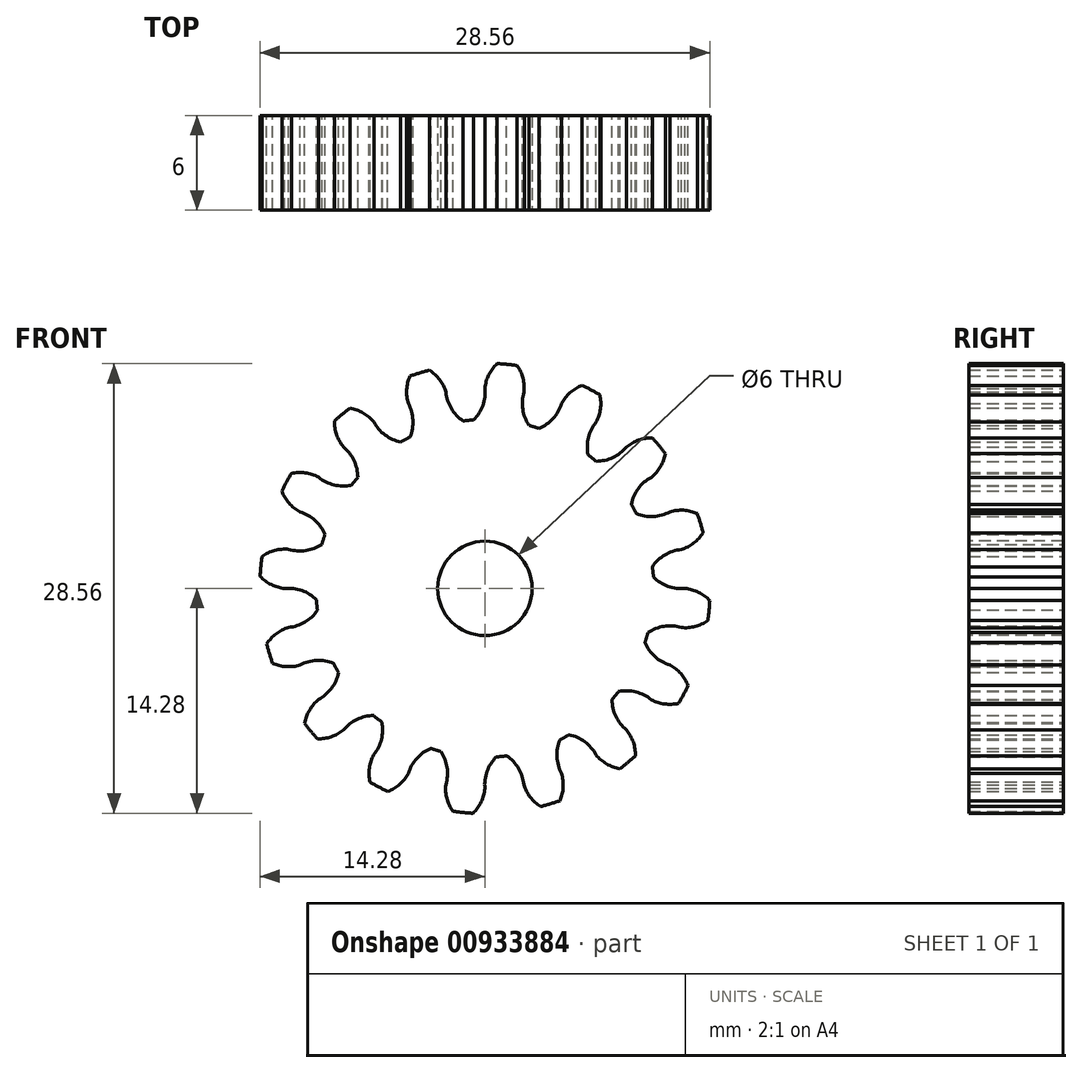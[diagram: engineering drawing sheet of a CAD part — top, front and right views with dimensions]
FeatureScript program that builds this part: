
annotation { "Feature Type Name" : "Feature", "Feature Type Description" : "" }
export const myFeature = defineFeature(function(context is Context, id is Id, definition is map)
    precondition{}
    {
        {
            var Q0;
            Q0=qCreatedBy(makeId("Front.planeOp"),FACE);
            var sketch = newSketch(context, id + "F0", { "sketchPlane" : qUnion([Q0])});
            skArc(sketch, "E0", {"start": v(2.04, 14.15) * mm, "mid": v(1.4, 14.23) * mm, "end": v(0.77, 14.28) * mm});
            skCircle(sketch, "E1", {"center": v(0, 0) * mm, "radius": 10.73 * mm});
            skArc(sketch, "E2", {"start": v(2.49, 12.47) * mm, "mid": v(2.41, 13.35) * mm, "end": v(2.04, 14.15) * mm});
            skArc(sketch, "E3", {"start": v(2.49, 12.47) * mm, "mid": v(2.4, 11.38) * mm, "end": v(2.8, 10.35) * mm});
            skArc(sketch, "E4", {"start": v(-0.72, 10.7) * mm, "mid": v(-0.13, 11.63) * mm, "end": v(0, 12.71) * mm});
            skArc(sketch, "E5.trimOffspring", {"start": v(0.77, 14.28) * mm, "mid": v(0.24, 13.57) * mm, "end": v(0, 12.71) * mm});
            skArc(sketch, "E6.1.0", {"start": v(-3.53, 13.86) * mm, "mid": v(-4.15, 13.69) * mm, "end": v(-4.75, 13.49) * mm});
            skArc(sketch, "E6.1.1", {"start": v(-4.75, 13.49) * mm, "mid": v(-4.97, 12.63) * mm, "end": v(-4.86, 11.74) * mm});
            skArc(sketch, "E6.1.2", {"start": v(-4.76, 9.61) * mm, "mid": v(-4.57, 10.7) * mm, "end": v(-4.86, 11.74) * mm});
            skArc(sketch, "E6.1.3", {"start": v(-2.47, 12.47) * mm, "mid": v(-2.88, 13.26) * mm, "end": v(-3.53, 13.86) * mm});
            skArc(sketch, "E6.1.4", {"start": v(-2.47, 12.47) * mm, "mid": v(-2.13, 11.43) * mm, "end": v(-1.38, 10.64) * mm});
            skArc(sketch, "E6.2.0", {"start": v(-8.57, 11.45) * mm, "mid": v(-9.07, 11.06) * mm, "end": v(-9.55, 10.64) * mm});
            skArc(sketch, "E6.2.1", {"start": v(-9.55, 10.64) * mm, "mid": v(-9.42, 9.76) * mm, "end": v(-8.99, 8.99) * mm});
            skArc(sketch, "E6.2.2", {"start": v(-8.08, 7.06) * mm, "mid": v(-8.32, 8.13) * mm, "end": v(-8.99, 8.99) * mm});
            skArc(sketch, "E6.2.3", {"start": v(-7.06, 10.57) * mm, "mid": v(-7.73, 11.15) * mm, "end": v(-8.57, 11.45) * mm});
            skArc(sketch, "E6.2.4", {"start": v(-7.06, 10.57) * mm, "mid": v(-6.34, 9.74) * mm, "end": v(-5.34, 9.3) * mm});
            skArc(sketch, "E6.3.0", {"start": v(-12.3, 7.3) * mm, "mid": v(-12.61, 6.74) * mm, "end": v(-12.9, 6.17) * mm});
            skArc(sketch, "E6.3.1", {"start": v(-12.9, 6.17) * mm, "mid": v(-12.44, 5.42) * mm, "end": v(-11.74, 4.86) * mm});
            skArc(sketch, "E6.3.2", {"start": v(-10.16, 3.43) * mm, "mid": v(-10.8, 4.33) * mm, "end": v(-11.74, 4.86) * mm});
            skArc(sketch, "E6.3.3", {"start": v(-10.57, 7.07) * mm, "mid": v(-11.41, 7.34) * mm, "end": v(-12.3, 7.3) * mm});
            skArc(sketch, "E6.3.4", {"start": v(-10.57, 7.07) * mm, "mid": v(-9.59, 6.57) * mm, "end": v(-8.5, 6.55) * mm});
            skArc(sketch, "E6.4.0", {"start": v(-14.15, 2.04) * mm, "mid": v(-14.23, 1.4) * mm, "end": v(-14.28, 0.77) * mm});
            skArc(sketch, "E6.4.1", {"start": v(-14.28, 0.77) * mm, "mid": v(-13.57, 0.24) * mm, "end": v(-12.71, 0) * mm});
            skArc(sketch, "E6.4.2", {"start": v(-10.7, -0.72) * mm, "mid": v(-11.63, -0.13) * mm, "end": v(-12.71, 0) * mm});
            skArc(sketch, "E6.4.3", {"start": v(-12.47, 2.49) * mm, "mid": v(-13.35, 2.41) * mm, "end": v(-14.15, 2.04) * mm});
            skArc(sketch, "E6.4.4", {"start": v(-12.47, 2.49) * mm, "mid": v(-11.38, 2.4) * mm, "end": v(-10.35, 2.8) * mm});
            skArc(sketch, "E6.5.0", {"start": v(-13.86, -3.53) * mm, "mid": v(-13.69, -4.15) * mm, "end": v(-13.49, -4.75) * mm});
            skArc(sketch, "E6.5.1", {"start": v(-13.49, -4.75) * mm, "mid": v(-12.63, -4.97) * mm, "end": v(-11.74, -4.86) * mm});
            skArc(sketch, "E6.5.2", {"start": v(-9.61, -4.76) * mm, "mid": v(-10.7, -4.57) * mm, "end": v(-11.74, -4.86) * mm});
            skArc(sketch, "E6.5.3", {"start": v(-12.47, -2.47) * mm, "mid": v(-13.26, -2.88) * mm, "end": v(-13.86, -3.53) * mm});
            skArc(sketch, "E6.5.4", {"start": v(-12.47, -2.47) * mm, "mid": v(-11.43, -2.13) * mm, "end": v(-10.64, -1.38) * mm});
            skArc(sketch, "E6.6.0", {"start": v(-11.45, -8.57) * mm, "mid": v(-11.06, -9.07) * mm, "end": v(-10.64, -9.55) * mm});
            skArc(sketch, "E6.6.1", {"start": v(-10.64, -9.55) * mm, "mid": v(-9.76, -9.42) * mm, "end": v(-8.99, -8.99) * mm});
            skArc(sketch, "E6.6.2", {"start": v(-7.06, -8.08) * mm, "mid": v(-8.13, -8.32) * mm, "end": v(-8.99, -8.99) * mm});
            skArc(sketch, "E6.6.3", {"start": v(-10.57, -7.06) * mm, "mid": v(-11.15, -7.73) * mm, "end": v(-11.45, -8.57) * mm});
            skArc(sketch, "E6.6.4", {"start": v(-10.57, -7.06) * mm, "mid": v(-9.74, -6.34) * mm, "end": v(-9.3, -5.34) * mm});
            skArc(sketch, "E6.7.0", {"start": v(-7.3, -12.3) * mm, "mid": v(-6.74, -12.61) * mm, "end": v(-6.17, -12.9) * mm});
            skArc(sketch, "E6.7.1", {"start": v(-6.17, -12.9) * mm, "mid": v(-5.42, -12.44) * mm, "end": v(-4.86, -11.74) * mm});
            skArc(sketch, "E6.7.2", {"start": v(-3.43, -10.16) * mm, "mid": v(-4.33, -10.8) * mm, "end": v(-4.86, -11.74) * mm});
            skArc(sketch, "E6.7.3", {"start": v(-7.07, -10.57) * mm, "mid": v(-7.34, -11.41) * mm, "end": v(-7.3, -12.3) * mm});
            skArc(sketch, "E6.7.4", {"start": v(-7.07, -10.57) * mm, "mid": v(-6.57, -9.59) * mm, "end": v(-6.55, -8.5) * mm});
            skArc(sketch, "E6.8.0", {"start": v(-2.04, -14.15) * mm, "mid": v(-1.4, -14.23) * mm, "end": v(-0.77, -14.28) * mm});
            skArc(sketch, "E6.8.1", {"start": v(-0.77, -14.28) * mm, "mid": v(-0.24, -13.57) * mm, "end": v(0, -12.71) * mm});
            skArc(sketch, "E6.8.2", {"start": v(0.72, -10.7) * mm, "mid": v(0.13, -11.63) * mm, "end": v(0, -12.71) * mm});
            skArc(sketch, "E6.8.3", {"start": v(-2.49, -12.47) * mm, "mid": v(-2.41, -13.35) * mm, "end": v(-2.04, -14.15) * mm});
            skArc(sketch, "E6.8.4", {"start": v(-2.49, -12.47) * mm, "mid": v(-2.4, -11.38) * mm, "end": v(-2.8, -10.35) * mm});
            skArc(sketch, "E6.9.0", {"start": v(3.53, -13.86) * mm, "mid": v(4.15, -13.69) * mm, "end": v(4.75, -13.49) * mm});
            skArc(sketch, "E6.9.1", {"start": v(4.75, -13.49) * mm, "mid": v(4.97, -12.63) * mm, "end": v(4.86, -11.74) * mm});
            skArc(sketch, "E6.9.2", {"start": v(4.76, -9.61) * mm, "mid": v(4.57, -10.7) * mm, "end": v(4.86, -11.74) * mm});
            skArc(sketch, "E6.9.3", {"start": v(2.47, -12.47) * mm, "mid": v(2.88, -13.26) * mm, "end": v(3.53, -13.86) * mm});
            skArc(sketch, "E6.9.4", {"start": v(2.47, -12.47) * mm, "mid": v(2.13, -11.43) * mm, "end": v(1.38, -10.64) * mm});
            skArc(sketch, "E6.10.0", {"start": v(8.57, -11.45) * mm, "mid": v(9.07, -11.06) * mm, "end": v(9.55, -10.64) * mm});
            skArc(sketch, "E6.10.1", {"start": v(9.55, -10.64) * mm, "mid": v(9.42, -9.76) * mm, "end": v(8.99, -8.99) * mm});
            skArc(sketch, "E6.10.2", {"start": v(8.08, -7.06) * mm, "mid": v(8.32, -8.13) * mm, "end": v(8.99, -8.99) * mm});
            skArc(sketch, "E6.10.3", {"start": v(7.06, -10.57) * mm, "mid": v(7.73, -11.15) * mm, "end": v(8.57, -11.45) * mm});
            skArc(sketch, "E6.10.4", {"start": v(7.06, -10.57) * mm, "mid": v(6.34, -9.74) * mm, "end": v(5.34, -9.3) * mm});
            skArc(sketch, "E6.11.0", {"start": v(12.3, -7.3) * mm, "mid": v(12.61, -6.74) * mm, "end": v(12.9, -6.17) * mm});
            skArc(sketch, "E6.11.1", {"start": v(12.9, -6.17) * mm, "mid": v(12.44, -5.42) * mm, "end": v(11.74, -4.86) * mm});
            skArc(sketch, "E6.11.2", {"start": v(10.16, -3.43) * mm, "mid": v(10.8, -4.33) * mm, "end": v(11.74, -4.86) * mm});
            skArc(sketch, "E6.11.3", {"start": v(10.57, -7.07) * mm, "mid": v(11.41, -7.34) * mm, "end": v(12.3, -7.3) * mm});
            skArc(sketch, "E6.11.4", {"start": v(10.57, -7.07) * mm, "mid": v(9.59, -6.57) * mm, "end": v(8.5, -6.55) * mm});
            skArc(sketch, "E6.12.0", {"start": v(14.15, -2.04) * mm, "mid": v(14.23, -1.4) * mm, "end": v(14.28, -0.77) * mm});
            skArc(sketch, "E6.12.1", {"start": v(14.28, -0.77) * mm, "mid": v(13.57, -0.24) * mm, "end": v(12.71, 0) * mm});
            skArc(sketch, "E6.12.2", {"start": v(10.7, 0.72) * mm, "mid": v(11.63, 0.13) * mm, "end": v(12.71, 0) * mm});
            skArc(sketch, "E6.12.3", {"start": v(12.47, -2.49) * mm, "mid": v(13.35, -2.41) * mm, "end": v(14.15, -2.04) * mm});
            skArc(sketch, "E6.12.4", {"start": v(12.47, -2.49) * mm, "mid": v(11.38, -2.4) * mm, "end": v(10.35, -2.8) * mm});
            skArc(sketch, "E6.13.0", {"start": v(13.86, 3.53) * mm, "mid": v(13.69, 4.15) * mm, "end": v(13.49, 4.75) * mm});
            skArc(sketch, "E6.13.1", {"start": v(13.49, 4.75) * mm, "mid": v(12.63, 4.97) * mm, "end": v(11.74, 4.86) * mm});
            skArc(sketch, "E6.13.2", {"start": v(9.61, 4.76) * mm, "mid": v(10.7, 4.57) * mm, "end": v(11.74, 4.86) * mm});
            skArc(sketch, "E6.13.3", {"start": v(12.47, 2.47) * mm, "mid": v(13.26, 2.88) * mm, "end": v(13.86, 3.53) * mm});
            skArc(sketch, "E6.13.4", {"start": v(12.47, 2.47) * mm, "mid": v(11.43, 2.13) * mm, "end": v(10.64, 1.38) * mm});
            skArc(sketch, "E6.14.0", {"start": v(11.45, 8.57) * mm, "mid": v(11.06, 9.07) * mm, "end": v(10.64, 9.55) * mm});
            skArc(sketch, "E6.14.1", {"start": v(10.64, 9.55) * mm, "mid": v(9.76, 9.42) * mm, "end": v(8.99, 8.99) * mm});
            skArc(sketch, "E6.14.2", {"start": v(7.06, 8.08) * mm, "mid": v(8.13, 8.32) * mm, "end": v(8.99, 8.99) * mm});
            skArc(sketch, "E6.14.3", {"start": v(10.57, 7.06) * mm, "mid": v(11.15, 7.73) * mm, "end": v(11.45, 8.57) * mm});
            skArc(sketch, "E6.14.4", {"start": v(10.57, 7.06) * mm, "mid": v(9.74, 6.34) * mm, "end": v(9.3, 5.34) * mm});
            skArc(sketch, "E6.15.0", {"start": v(7.3, 12.3) * mm, "mid": v(6.74, 12.61) * mm, "end": v(6.17, 12.9) * mm});
            skArc(sketch, "E6.15.1", {"start": v(6.17, 12.9) * mm, "mid": v(5.42, 12.44) * mm, "end": v(4.86, 11.74) * mm});
            skArc(sketch, "E6.15.2", {"start": v(3.43, 10.16) * mm, "mid": v(4.33, 10.8) * mm, "end": v(4.86, 11.74) * mm});
            skArc(sketch, "E6.15.3", {"start": v(7.07, 10.57) * mm, "mid": v(7.34, 11.41) * mm, "end": v(7.3, 12.3) * mm});
            skArc(sketch, "E6.15.4", {"start": v(7.07, 10.57) * mm, "mid": v(6.57, 9.59) * mm, "end": v(6.55, 8.5) * mm});
            skSolve(sketch);
        }
        {
            var Q0;
            Q0 = qSketchRegion(id + "F0", true);
            extrude(context, id + "F1", {"entities" : qUnion([Q0]), "depth" : 6 * mm, "offsetDistance" : 25 * mm});
        }
        {
            var Q0;
            Q0=makeQuery(id+"F1.opExtrude","CAP_FACE",FACE,{"disambiguationData":[OSD([sQuery(id+"F0.wireOp",EDGE,"E0"),sQuery(id+"F0.wireOp",EDGE,"E2"),sQuery(id+"F0.wireOp",EDGE,"E3"),sQuery(id+"F0.wireOp",EDGE,"E4"),sQuery(id+"F0.wireOp",EDGE,"E5.trimOffspring"),sQuery(id+"F0.wireOp",EDGE,"E6.1.0"),sQuery(id+"F0.wireOp",EDGE,"E6.1.1"),sQuery(id+"F0.wireOp",EDGE,"E6.1.2"),sQuery(id+"F0.wireOp",EDGE,"E6.1.3"),sQuery(id+"F0.wireOp",EDGE,"E6.1.4"),sQuery(id+"F0.wireOp",EDGE,"E6.2.0"),sQuery(id+"F0.wireOp",EDGE,"E6.2.1"),sQuery(id+"F0.wireOp",EDGE,"E6.2.2"),sQuery(id+"F0.wireOp",EDGE,"E6.2.3"),sQuery(id+"F0.wireOp",EDGE,"E6.2.4"),sQuery(id+"F0.wireOp",EDGE,"E6.3.0"),sQuery(id+"F0.wireOp",EDGE,"E6.3.1"),sQuery(id+"F0.wireOp",EDGE,"E6.3.2"),sQuery(id+"F0.wireOp",EDGE,"E6.3.3"),sQuery(id+"F0.wireOp",EDGE,"E6.3.4"),sQuery(id+"F0.wireOp",EDGE,"E6.4.0"),sQuery(id+"F0.wireOp",EDGE,"E6.4.1"),sQuery(id+"F0.wireOp",EDGE,"E6.4.2"),sQuery(id+"F0.wireOp",EDGE,"E6.4.3"),sQuery(id+"F0.wireOp",EDGE,"E6.4.4"),sQuery(id+"F0.wireOp",EDGE,"E6.5.0"),sQuery(id+"F0.wireOp",EDGE,"E6.5.1"),sQuery(id+"F0.wireOp",EDGE,"E6.5.2"),sQuery(id+"F0.wireOp",EDGE,"E6.5.3"),sQuery(id+"F0.wireOp",EDGE,"E6.5.4"),sQuery(id+"F0.wireOp",EDGE,"E6.6.0"),sQuery(id+"F0.wireOp",EDGE,"E6.6.1"),sQuery(id+"F0.wireOp",EDGE,"E6.6.2"),sQuery(id+"F0.wireOp",EDGE,"E6.6.3"),sQuery(id+"F0.wireOp",EDGE,"E6.6.4"),sQuery(id+"F0.wireOp",EDGE,"E6.7.0"),sQuery(id+"F0.wireOp",EDGE,"E6.7.1"),sQuery(id+"F0.wireOp",EDGE,"E6.7.2"),sQuery(id+"F0.wireOp",EDGE,"E6.7.3"),sQuery(id+"F0.wireOp",EDGE,"E6.7.4"),sQuery(id+"F0.wireOp",EDGE,"E6.8.0"),sQuery(id+"F0.wireOp",EDGE,"E6.8.1"),sQuery(id+"F0.wireOp",EDGE,"E6.8.2"),sQuery(id+"F0.wireOp",EDGE,"E6.8.3"),sQuery(id+"F0.wireOp",EDGE,"E6.8.4"),sQuery(id+"F0.wireOp",EDGE,"E6.9.0"),sQuery(id+"F0.wireOp",EDGE,"E6.9.1"),sQuery(id+"F0.wireOp",EDGE,"E6.9.2"),sQuery(id+"F0.wireOp",EDGE,"E6.9.3"),sQuery(id+"F0.wireOp",EDGE,"E6.9.4"),sQuery(id+"F0.wireOp",EDGE,"E6.10.0"),sQuery(id+"F0.wireOp",EDGE,"E6.10.1"),sQuery(id+"F0.wireOp",EDGE,"E6.10.2"),sQuery(id+"F0.wireOp",EDGE,"E6.10.3"),sQuery(id+"F0.wireOp",EDGE,"E6.10.4"),sQuery(id+"F0.wireOp",EDGE,"E6.11.0"),sQuery(id+"F0.wireOp",EDGE,"E6.11.1"),sQuery(id+"F0.wireOp",EDGE,"E6.11.2"),sQuery(id+"F0.wireOp",EDGE,"E6.11.3"),sQuery(id+"F0.wireOp",EDGE,"E6.11.4"),sQuery(id+"F0.wireOp",EDGE,"E6.12.0"),sQuery(id+"F0.wireOp",EDGE,"E6.12.1"),sQuery(id+"F0.wireOp",EDGE,"E6.12.2"),sQuery(id+"F0.wireOp",EDGE,"E6.12.3"),sQuery(id+"F0.wireOp",EDGE,"E6.12.4"),sQuery(id+"F0.wireOp",EDGE,"E6.13.0"),sQuery(id+"F0.wireOp",EDGE,"E6.13.1"),sQuery(id+"F0.wireOp",EDGE,"E6.13.2"),sQuery(id+"F0.wireOp",EDGE,"E6.13.3"),sQuery(id+"F0.wireOp",EDGE,"E6.13.4"),sQuery(id+"F0.wireOp",EDGE,"E6.14.0"),sQuery(id+"F0.wireOp",EDGE,"E6.14.1"),sQuery(id+"F0.wireOp",EDGE,"E6.14.2"),sQuery(id+"F0.wireOp",EDGE,"E6.14.3"),sQuery(id+"F0.wireOp",EDGE,"E6.14.4"),sQuery(id+"F0.wireOp",EDGE,"E6.15.0"),sQuery(id+"F0.wireOp",EDGE,"E6.15.1"),sQuery(id+"F0.wireOp",EDGE,"E6.15.2"),sQuery(id+"F0.wireOp",EDGE,"E6.15.3"),sQuery(id+"F0.wireOp",EDGE,"E6.15.4"),sQuery(id+"F0.wireOp",EDGE,"E1")])],"isStart":false});
            var sketch = newSketch(context, id + "F2", { "sketchPlane" : qUnion([Q0])});
            skCircle(sketch, "E7", {"center": v(0, 0) * mm, "radius": 3 * mm});
            skSolve(sketch);
        }
        {
            var Q0;
            Q0 = qSketchRegion(id + "F2", true);
            extrude(context, id + "F3", {"entities" : qUnion([Q0]), "operationType" : NewBodyOperationType.REMOVE, "endBound" : BoundingType.THROUGH_ALL, "oppositeDirection" : true, "depth" : 25 * mm, "offsetDistance" : 25 * mm});
        }
    });
